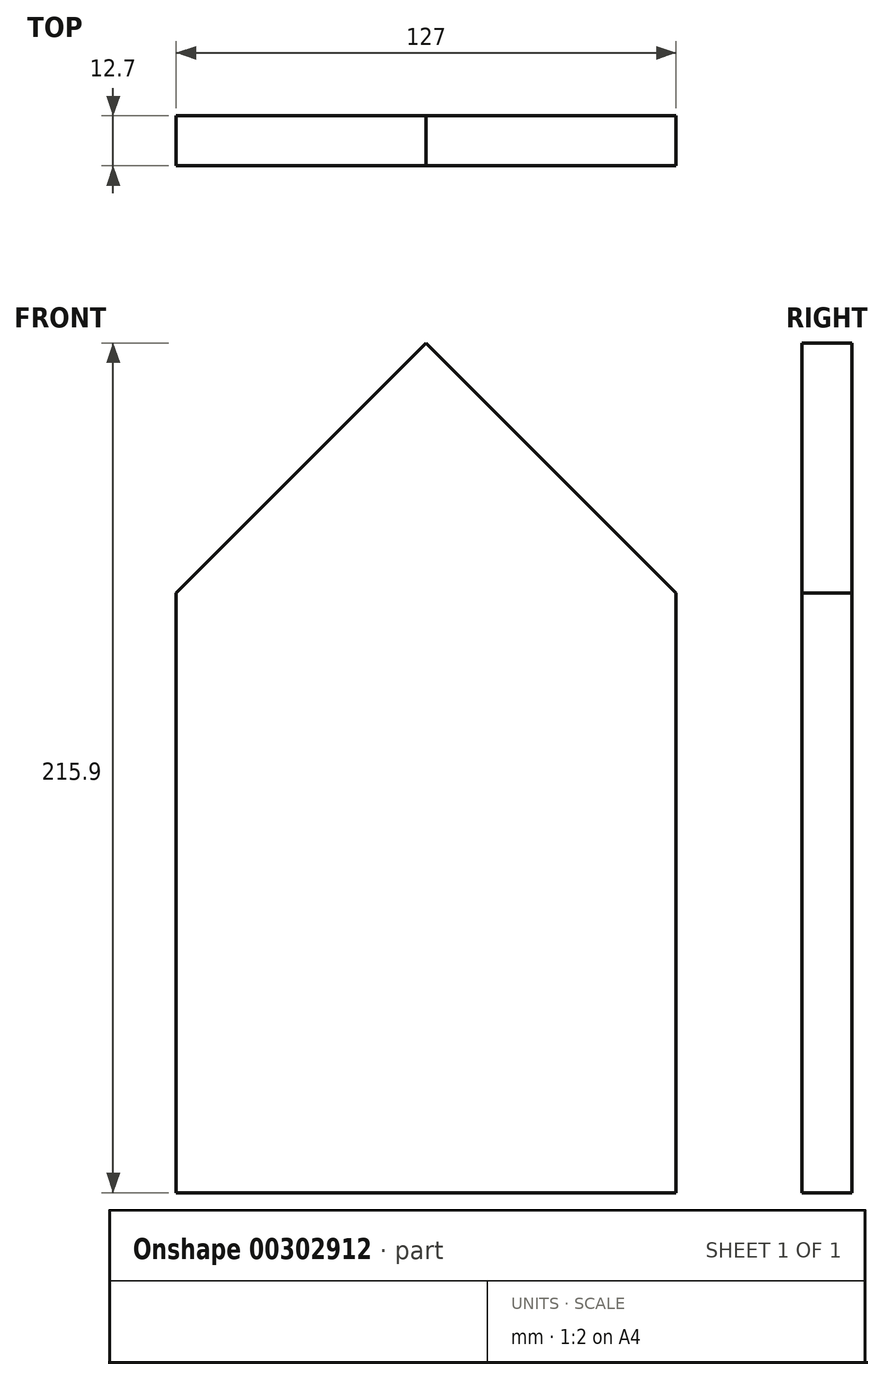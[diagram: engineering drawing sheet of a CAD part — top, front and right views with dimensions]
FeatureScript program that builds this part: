
annotation { "Feature Type Name" : "Feature", "Feature Type Description" : "" }
export const myFeature = defineFeature(function(context is Context, id is Id, definition is map)
    precondition{}
    {
        {
            var Q0;
            Q0=qCreatedBy(makeId("Front.planeOp"),FACE);
            var sketch = newSketch(context, id + "F0", { "sketchPlane" : qUnion([Q0])});
            skLineSegment(sketch, "E0.bottom", {"start": v(63.5, 76.2) * mm, "end": v(-63.5, 76.2) * mm, "construction": true});
            skLineSegment(sketch, "E0.top", {"start": v(63.5, -76.2) * mm, "end": v(-63.5, -76.2) * mm});
            skLineSegment(sketch, "E0.left", {"start": v(63.5, 76.2) * mm, "end": v(63.5, -76.2) * mm});
            skLineSegment(sketch, "E0.right", {"start": v(-63.5, 76.2) * mm, "end": v(-63.5, -76.2) * mm});
            skPoint(sketch, "E0.middle", {"position": v(0, 0) * mm});
            skLineSegment(sketch, "E1", {"start": v(-63.5, 76.2) * mm, "end": v(0, 139.7) * mm});
            skLineSegment(sketch, "E2", {"start": v(0, 139.7) * mm, "end": v(63.5, 76.2) * mm});
            skLineSegment(sketch, "E3", {"start": v(0, 139.7) * mm, "end": v(0, 76.2) * mm, "construction": true});
            skSolve(sketch);
        }
        {
            var Q0;
            Q0=makeQuery(id+"F0.imprint","IMPRINT",FACE,{"disambiguationData":[TD([[makeQuery(id+"F0.imprint","IMPRINT",EDGE,{"derivedFrom":sQuery(id+"F0.wireOp",EDGE,"E0.top")}),-1.0]])]});
            extrude(context, id + "F1", {"entities" : qUnion([Q0]), "depth" : 12.7 * mm});
        }
    });
